# Revit family: Haworth_Patterns_Cushion
name_source: partatom
category: Furniture Systems
revit_build: Autodesk Revit 2018 (Build: 20170223_1515(x64)
units: mm (PartAtom-declared; Revit-internal decimal feet)

## family parameters
Always vertical = Yes
Cut with Voids When Loaded = No
OmniClass Number = 23.40.70.14.64.21
OmniClass Title = Systems Furniture
Part Type = Normal
Room Calculation Point = No
Round Connector Dimension = Use Diameter
Shared = No
Work Plane-Based = No

## types (1)
- 35w 16-3/4d
    Actual Depth = 18"
    Actual Width = 35"
    Cushion Finish = Haworth _ Fabric _ Tellure _ Ivory 3A-35
    Custom Size = Yes
    Depth = 16 3/4"
    Description = Haworth - Patterns Storage - Accessories - Cushion
    Manufacturer = Haworth
    Max. Depth = 30"
    Max. Width = 36"
    Min. Depth = 18"
    Min. Width = 16"
    Model = Haworth - Patterns Storage - Accessories - Cushion
    Revision Number = 3
    Size = Verify Final Dim. w/ Haworth
    Standard Depths = 18, 24, 30 in.
    Standard Widths = 16, 30, 36 in.
    Sustainability Info = http://www.haworth.com
    Top Thickness = 1 3/16"
    URL = https://www.haworth.com
    URL - Product = https://www.haworth.com
    Warranty = http://www.haworth.com
    Width = 35"

## geometry (parser evidence)
native form markers: Sweep x3
no freeform markers — native parametric forms only
